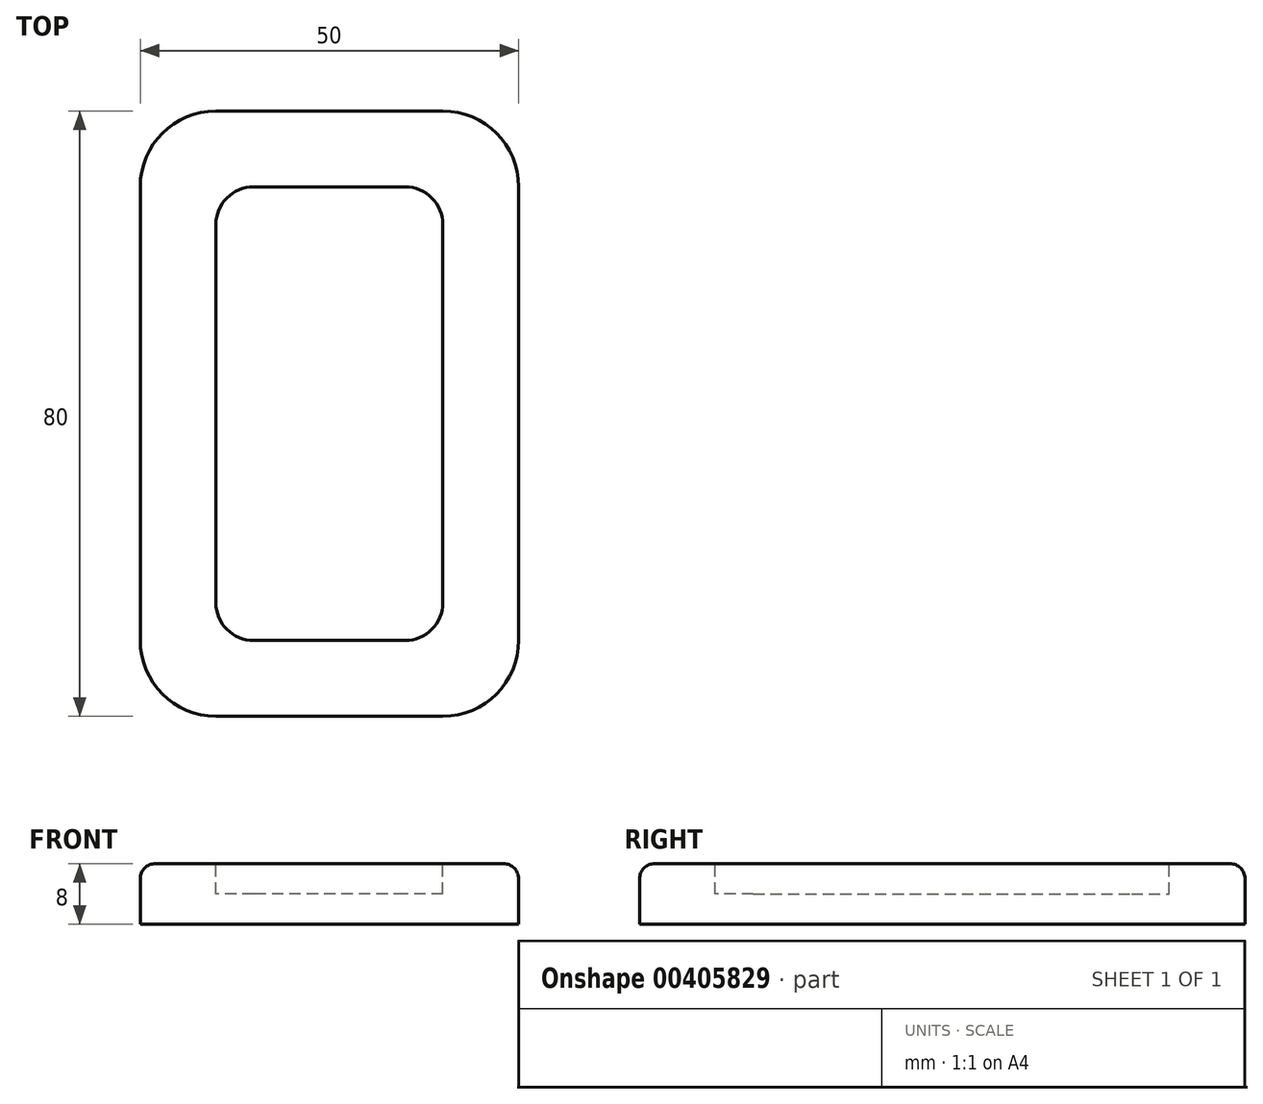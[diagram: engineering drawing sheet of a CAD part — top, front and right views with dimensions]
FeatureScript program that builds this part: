
annotation { "Feature Type Name" : "Feature", "Feature Type Description" : "" }
export const myFeature = defineFeature(function(context is Context, id is Id, definition is map)
    precondition{}
    {
        {
            var Q0;
            Q0=qCreatedBy(makeId("Top.planeOp"),FACE);
            var sketch = newSketch(context, id + "F0", { "sketchPlane" : qUnion([Q0])});
            skLineSegment(sketch, "E0.bottom", {"start": v(15, -40) * mm, "end": v(-15, -40) * mm});
            skLineSegment(sketch, "E0.top", {"start": v(15, 40) * mm, "end": v(-15, 40) * mm});
            skLineSegment(sketch, "E0.left", {"start": v(25, -30) * mm, "end": v(25, 30) * mm});
            skLineSegment(sketch, "E0.right", {"start": v(-25, -30) * mm, "end": v(-25, 30) * mm});
            skPoint(sketch, "E0.middle", {"position": v(0, 0) * mm});
            skPoint(sketch, "E1.visualSharp", {"position": v(-25, 40) * mm});
            skArc(sketch, "E1.filletArc", {"start": v(-15, 40) * mm, "mid": v(-22.07, 37.07) * mm, "end": v(-25, 30) * mm});
            skPoint(sketch, "E2.visualSharp", {"position": v(25, 40) * mm});
            skArc(sketch, "E2.filletArc", {"start": v(25, 30) * mm, "mid": v(22.07, 37.07) * mm, "end": v(15, 40) * mm});
            skPoint(sketch, "E3.visualSharp", {"position": v(-25, -40) * mm});
            skArc(sketch, "E3.filletArc", {"start": v(-25, -30) * mm, "mid": v(-22.07, -37.07) * mm, "end": v(-15, -40) * mm});
            skPoint(sketch, "E4.visualSharp", {"position": v(25, -40) * mm});
            skArc(sketch, "E4.filletArc", {"start": v(15, -40) * mm, "mid": v(22.07, -37.07) * mm, "end": v(25, -30) * mm});
            skSolve(sketch);
        }
        {
            var Q0;
            Q0=makeQuery(id+"F0.imprint","IMPRINT",FACE,{"disambiguationData":[TD([[makeQuery(id+"F0.imprint","IMPRINT",EDGE,{"derivedFrom":sQuery(id+"F0.wireOp",EDGE,"E0.bottom")}),-1.0]])]});
            extrude(context, id + "F1", {"entities" : qUnion([Q0]), "depth" : 8 * mm});
        }
        {
            var Q0;
            Q0=makeQuery(id+"F1.opExtrude","CAP_FACE",FACE,{"disambiguationData":[OSD([sQuery(id+"F0.wireOp",EDGE,"E0.bottom"),sQuery(id+"F0.wireOp",EDGE,"E0.top"),sQuery(id+"F0.wireOp",EDGE,"E0.left"),sQuery(id+"F0.wireOp",EDGE,"E0.right"),sQuery(id+"F0.wireOp",EDGE,"E1.filletArc"),sQuery(id+"F0.wireOp",EDGE,"E2.filletArc"),sQuery(id+"F0.wireOp",EDGE,"E3.filletArc"),sQuery(id+"F0.wireOp",EDGE,"E4.filletArc")])],"isStart":false});
            fillet(context, id + "F2", {"entities" : qUnion([Q0]), "radius" : 2 * mm, "tangentPropagation" : true, "allowEdgeOverflow" : false});
        }
        {
            var Q0;
            Q0=makeQuery(id+"F1.opExtrude","CAP_FACE",FACE,{"disambiguationData":[OSD([sQuery(id+"F0.wireOp",EDGE,"E0.bottom"),sQuery(id+"F0.wireOp",EDGE,"E0.top"),sQuery(id+"F0.wireOp",EDGE,"E0.left"),sQuery(id+"F0.wireOp",EDGE,"E0.right"),sQuery(id+"F0.wireOp",EDGE,"E1.filletArc"),sQuery(id+"F0.wireOp",EDGE,"E2.filletArc"),sQuery(id+"F0.wireOp",EDGE,"E3.filletArc"),sQuery(id+"F0.wireOp",EDGE,"E4.filletArc")])],"isStart":false});
            var sketch = newSketch(context, id + "F3", { "sketchPlane" : qUnion([Q0])});
            skLineSegment(sketch, "E5.bottom", {"start": v(10, -30) * mm, "end": v(-10, -30) * mm});
            skLineSegment(sketch, "E5.top", {"start": v(10, 30) * mm, "end": v(-10, 30) * mm});
            skLineSegment(sketch, "E5.left", {"start": v(15, -25) * mm, "end": v(15, 25) * mm});
            skLineSegment(sketch, "E5.right", {"start": v(-15, -25) * mm, "end": v(-15, 25) * mm});
            skPoint(sketch, "E5.middle", {"position": v(0, 0) * mm});
            skPoint(sketch, "E6.visualSharp", {"position": v(-15, 30) * mm});
            skArc(sketch, "E6.filletArc", {"start": v(-10, 30) * mm, "mid": v(-13.54, 28.54) * mm, "end": v(-15, 25) * mm});
            skPoint(sketch, "E7.visualSharp", {"position": v(15, 30) * mm});
            skArc(sketch, "E7.filletArc", {"start": v(15, 25) * mm, "mid": v(13.54, 28.54) * mm, "end": v(10, 30) * mm});
            skPoint(sketch, "E8.visualSharp", {"position": v(15, -30) * mm});
            skArc(sketch, "E8.filletArc", {"start": v(10, -30) * mm, "mid": v(13.54, -28.54) * mm, "end": v(15, -25) * mm});
            skPoint(sketch, "E9.visualSharp", {"position": v(-15, -30) * mm});
            skArc(sketch, "E9.filletArc", {"start": v(-15, -25) * mm, "mid": v(-13.54, -28.54) * mm, "end": v(-10, -30) * mm});
            skSolve(sketch);
        }
        {
            var Q0;
            Q0 = qSketchRegion(id + "F3", true);
            extrude(context, id + "F4", {"entities" : qUnion([Q0]), "operationType" : NewBodyOperationType.REMOVE, "oppositeDirection" : true, "depth" : 4 * mm});
        }
    });
